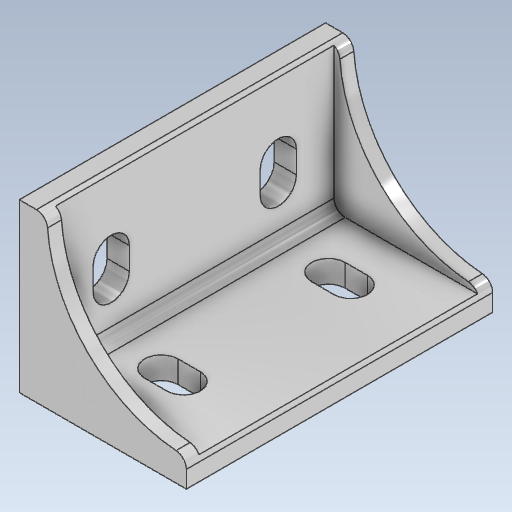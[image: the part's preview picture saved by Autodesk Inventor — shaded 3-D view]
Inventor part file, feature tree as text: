
AUTODESK INVENTOR PART (.ipt)
format: ipt  version: 2020.2 (Build 242310000, 310)  size: 230,912 bytes
history: native  units: mm
features: extrude x5, sketch x3, fillet x1
ambient origin geometry x8: Origin, YZ Plane, XZ Plane, XY Plane, X Axis, Y Axis, Z Axis, Center Point
bodies: Solid1 (feature_tree)
feature tree (9):
  sketch  "Sketch1"  dims[d2=26.0mm d3=26.0mm]
  extrude  "Extrusion1"  Depth=26.0mm
  extrude  "Extrusion2"  Depth=1.0mm
  extrude  "Extrusion3"  Depth=2.0mm
  extrude  "Extrusion4"  Depth=50.0mm TaperAngle=0.0deg
  fillet  "Fillet1"  Radius=2.5mm
  extrude  "Extrusion5"  Depth=2.5mm TaperAngle=0.0deg
  sketch  "Sketch2"  dims[d4=1.0mm d5=1.0mm]
  sketch  "Sketch3"  dims[d6=25.0mm d7=2.0mm d8=50.0mm d9=0.0mm d10=2.5mm d11=0.0mm d12=2.5mm d13=0.0mm d14=15.0mm d15=12.5mm d16=30.0mm d17=2.0mm d18=6.0mm d19=2.0mm d20=6.0mm d21=4.0mm d22=0.0mm d23=2.0mm d31=15.0mm d32=12.5mm d33=30.0mm d34=2.0mm d35=6.5mm d36=2.0mm d37=6.5mm d38=4.0mm d39=0.0mm]
